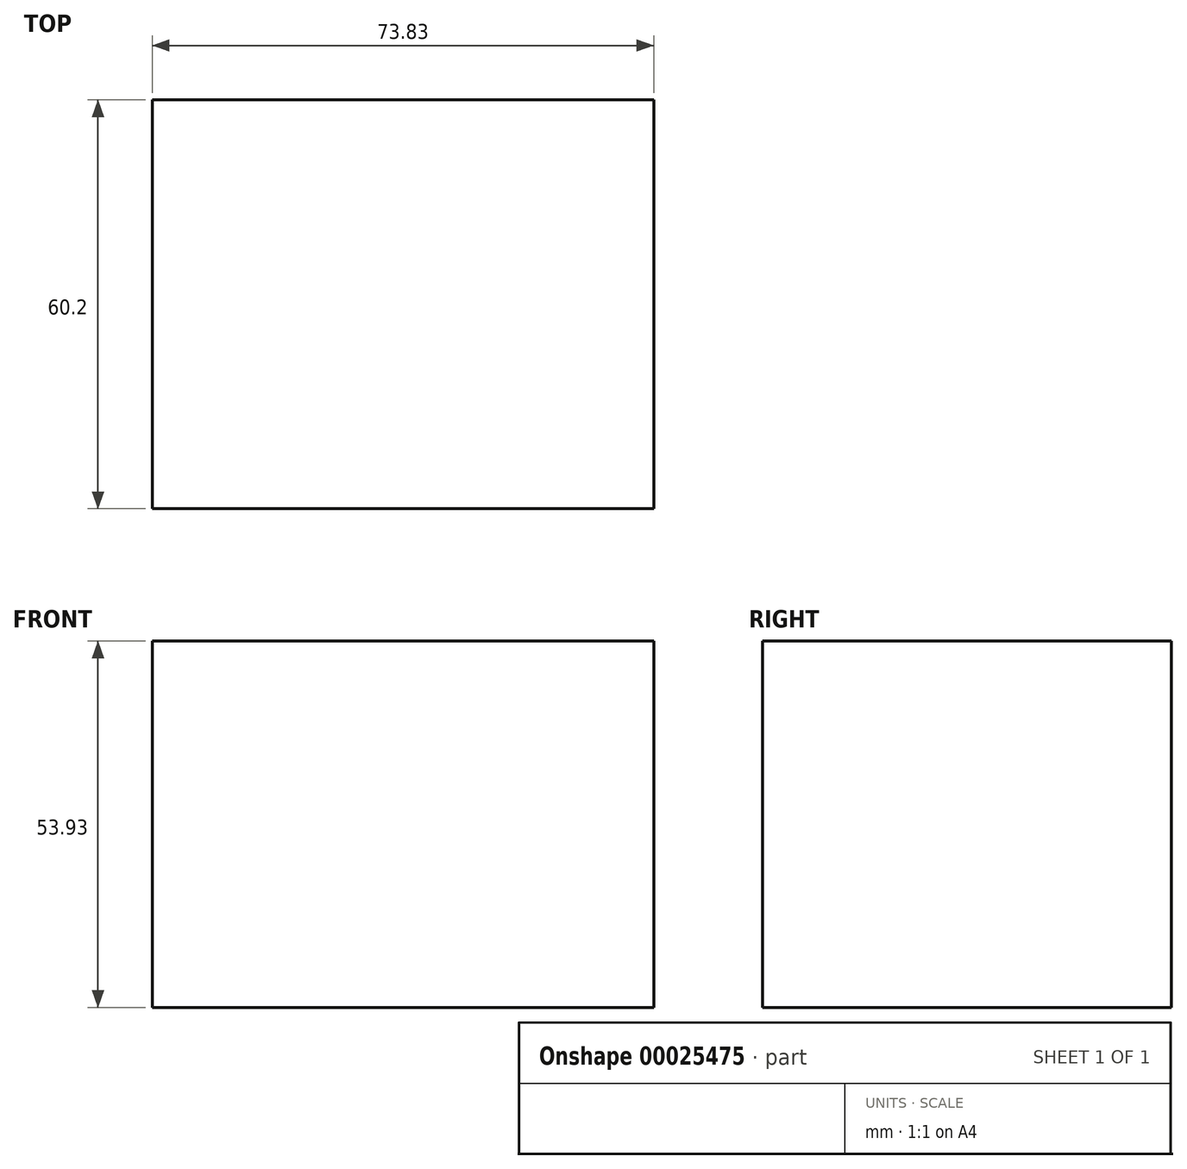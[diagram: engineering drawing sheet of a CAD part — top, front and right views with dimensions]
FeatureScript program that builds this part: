
annotation { "Feature Type Name" : "Feature", "Feature Type Description" : "" }
export const myFeature = defineFeature(function(context is Context, id is Id, definition is map)
    precondition{}
    {
        {
            var Q0;
            Q0=qCreatedBy(makeId("Top.planeOp"),FACE);
            var sketch = newSketch(context, id + "F0", { "sketchPlane" : qUnion([Q0])});
            skLineSegment(sketch, "E0.bottom", {"start": v(-38.46, 25.47) * mm, "end": v(35.37, 25.47) * mm});
            skLineSegment(sketch, "E0.top", {"start": v(-38.46, -34.73) * mm, "end": v(35.37, -34.73) * mm});
            skLineSegment(sketch, "E0.left", {"start": v(-38.46, 25.47) * mm, "end": v(-38.46, -34.73) * mm});
            skLineSegment(sketch, "E0.right", {"start": v(35.37, 25.47) * mm, "end": v(35.37, -34.73) * mm});
            skSolve(sketch);
        }
        {
            var Q0;
            Q0=makeQuery(id+"F0.imprint","IMPRINT",FACE,{"disambiguationData":[TD([[makeQuery(id+"F0.imprint","IMPRINT",EDGE,{"derivedFrom":sQuery(id+"F0.wireOp",EDGE,"E0.bottom")}),-1.0]])]});
            extrude(context, id + "F1", {"entities" : qUnion([Q0]), "depth" : 53.93 * mm});
        }
    });
